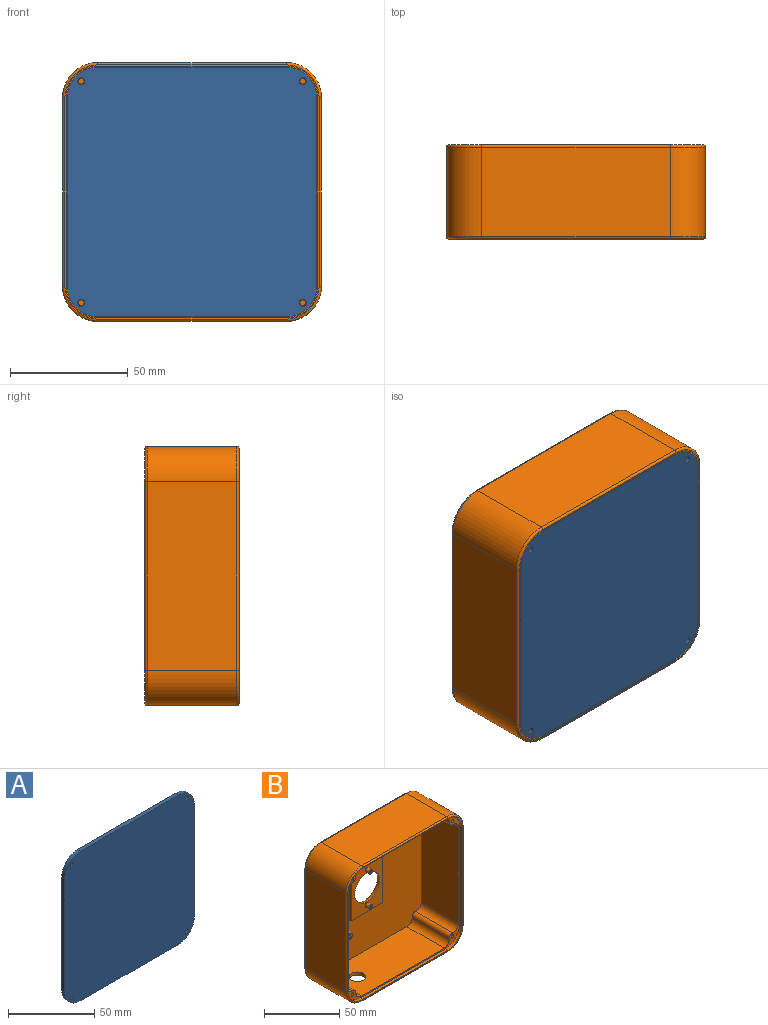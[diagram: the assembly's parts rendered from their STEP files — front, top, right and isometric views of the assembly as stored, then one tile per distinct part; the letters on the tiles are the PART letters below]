
ASSEMBLY  parts=2 mates=1
PART A: 14 faces, bbox 106x2.5x106 mm
  f0: plane 80x2.5mm, normal (-1,0,0), area 200mm2, adj f4,f5,f6,f9
  f1: plane 80x2.5mm, normal (0,0,-1), area 200mm2, adj f4,f5,f6,f7
  f2: plane 80x2.5mm, normal (1,0,0), area 200mm2, adj f4,f5,f7,f8
  f3: plane 80x2.5mm, normal (0,0,1), area 200mm2, adj f4,f5,f8,f9
  f4: plane 106x106mm, normal (0,-1,0), area 11062.7mm2, adj f0,f1,f2,f3,f6,f7,f8,f9
  f5: plane 106x106mm, normal (0,1,0), area 11062.7mm2, adj f0,f1,f2,f3,f6,f7,f8,f9
  f6: cylinder r=13mm len=13mm, axis (0,-1,0), area 51.1mm2, adj f0,f1,f4,f5
  f7: cylinder r=13mm len=13mm, axis (0,1,0), area 51.1mm2, adj f1,f2,f4,f5
  f8: cylinder r=13mm len=13mm, axis (0,-1,0), area 51.1mm2, adj f2,f3,f4,f5
  f9: cylinder r=13mm len=13mm, axis (0,1,0), area 51.1mm2, adj f0,f3,f4,f5
  f10: cylinder r=1.5mm len=3mm, axis (0,-1,0), area 23.6mm2, adj f4,f5
  f11: cylinder r=1.5mm len=3mm, axis (0,-1,0), area 23.6mm2, adj f4,f5
  f12: cylinder r=1.5mm len=3mm, axis (0,-1,0), area 23.6mm2, adj f4,f5
  f13: cylinder r=1.5mm len=3mm, axis (0,-1,0), area 23.6mm2, adj f4,f5
PART B: 91 faces, bbox 112.5x40x112.5 mm
  f0: cylinder r=3mm len=35mm, axis (0,1,0), area 176.2mm2, adj f1,f45,f83,f84
  f1: plane 107x107mm, normal (0,-1,0), area 566.8mm2, adj f0,f2,f4,f5,f7,f8,f9,f10
  f2: cylinder r=1.25mm len=35mm, axis (0,1,0), area 274.9mm2, adj f1,f82
  f3: plane 2.5x2.5mm, normal (0,-1,0), area 4.9mm2, adj f80
  f4: cylinder r=3mm len=35mm, axis (0,1,0), area 176.2mm2, adj f1,f45,f87,f88
  f5: cylinder r=1.25mm len=35mm, axis (0,1,0), area 274.9mm2, adj f1,f79
  f6: plane 2.5x2.5mm, normal (0,-1,0), area 4.9mm2, adj f77
  f7: plane 78.17x35mm, normal (0,0,-1), area 2735.8mm2, adj f1,f45,f88,f89
  f8: plane 78.17x35mm, normal (1,0,0), area 2735.8mm2, adj f1,f45,f86,f87
  f9: plane 78.17x35mm, normal (0,0,1), area 2640.7mm2, adj f1,f45,f54,f84,f85
  f10: plane 78.17x35mm, normal (-1,0,0), area 2735.8mm2, adj f1,f45,f83,f90
  f11: cone r=2.5mm half-angle=10deg, axis (0,1,0), area 151.3mm2, adj f12,f45
  f12: plane 5x5mm, normal (0,-1,0), area 14.7mm2, adj f11,f53
  f13: cone r=2.5mm half-angle=10deg, axis (0,1,0), area 151.3mm2, adj f14,f45
  f14: plane 5x5mm, normal (0,-1,0), area 14.7mm2, adj f13,f51
  f15: cone r=2.5mm half-angle=10deg, axis (0,1,0), area 151.3mm2, adj f16,f45
  f16: plane 5x5mm, normal (0,-1,0), area 14.7mm2, adj f15,f49
  f17: cone r=2.5mm half-angle=10deg, axis (0,1,0), area 151.3mm2, adj f18,f45
  f18: plane 5x5mm, normal (0,-1,0), area 14.7mm2, adj f17,f47
  f19: plane 80x38mm, normal (0,0,1), area 3040mm2, adj f25,f28,f35,f42
  f20: plane 80x38mm, normal (-1,0,0), area 3040mm2, adj f25,f26,f34,f43
  f21: plane 80x38mm, normal (0,0,-1), area 2945mm2, adj f26,f27,f30,f39,f54
  f22: plane 80x38mm, normal (1,0,0), area 3040mm2, adj f27,f28,f31,f38
  f23: plane 108x108mm, normal (0,1,0), area 10731.2mm2, adj f29,f30,f31,f32,f33,f34,f35,f36
  f24: plane 108x108mm, normal (0,-1,0), area 203.2mm2, adj f37,f38,f39,f40,f41,f42,f43,f44
  f25: cylinder r=15mm len=38mm, axis (0,1,0), area 895.4mm2, adj f19,f20,f36,f44
  f26: cylinder r=15mm len=38mm, axis (0,-1,0), area 895.4mm2, adj f20,f21,f32,f41
  f27: cylinder r=15mm len=38mm, axis (0,1,0), area 895.4mm2, adj f21,f22,f29,f37
  f28: cylinder r=15mm len=38mm, axis (0,-1,0), area 895.4mm2, adj f19,f22,f33,f40
  f29: torus R=14mm, axis (0,-1,0), area 36.1mm2, adj f23,f27,f30,f31
  f30: cylinder r=1mm len=80mm, axis (-1,0,0), area 125.7mm2, adj f21,f23,f29,f32
  f31: cylinder r=1mm len=80mm, axis (0,0,-1), area 125.7mm2, adj f22,f23,f29,f33
  f32: torus R=14mm, axis (0,-1,0), area 36.1mm2, adj f23,f26,f30,f34
  f33: torus R=14mm, axis (0,-1,0), area 36.1mm2, adj f23,f28,f31,f35
  f34: cylinder r=1mm len=80mm, axis (0,0,1), area 125.7mm2, adj f20,f23,f32,f36
  f35: cylinder r=1mm len=80mm, axis (1,0,0), area 125.7mm2, adj f19,f23,f33,f36
  f36: torus R=14mm, axis (0,-1,0), area 36.1mm2, adj f23,f25,f34,f35
  f37: torus R=14mm, axis (0,-1,0), area 36.1mm2, adj f24,f27,f38,f39
  f38: cylinder r=1mm len=80mm, axis (0,0,1), area 125.7mm2, adj f22,f24,f37,f40
  f39: cylinder r=1mm len=80mm, axis (1,0,0), area 125.7mm2, adj f21,f24,f37,f41
  f40: torus R=14mm, axis (0,-1,0), area 36.1mm2, adj f24,f28,f38,f42
  f41: torus R=14mm, axis (0,-1,0), area 36.1mm2, adj f24,f26,f39,f43
  f42: cylinder r=1mm len=80mm, axis (-1,0,0), area 125.7mm2, adj f19,f24,f40,f44
  f43: cylinder r=1mm len=80mm, axis (0,0,-1), area 125.7mm2, adj f20,f24,f41,f44
  f44: torus R=14mm, axis (0,-1,0), area 36.1mm2, adj f24,f25,f42,f43
  f45: plane 105x105mm, normal (0,-1,0), area 9322.5mm2, adj f0,f4,f7,f8,f9,f10,f11,f13
  f46: plane 2.5x2.5mm, normal (0,-1,0), area 4.9mm2, adj f47
  f47: cylinder r=1.25mm len=7.5mm, axis (0,-1,0), area 58.9mm2, adj f18,f46
  f48: plane 2.5x2.5mm, normal (0,-1,0), area 4.9mm2, adj f49
  f49: cylinder r=1.25mm len=7.5mm, axis (0,-1,0), area 58.9mm2, adj f16,f48
  f50: plane 2.5x2.5mm, normal (0,-1,0), area 4.9mm2, adj f51
  f51: cylinder r=1.25mm len=7.5mm, axis (0,-1,0), area 58.9mm2, adj f14,f50
  f52: plane 2.5x2.5mm, normal (0,-1,0), area 4.9mm2, adj f53
  f53: cylinder r=1.25mm len=7.5mm, axis (0,-1,0), area 58.9mm2, adj f12,f52
  f54: cylinder r=5.5mm len=11mm, axis (0,0,-1), area 86.4mm2, adj f9,f21
  f55: plane 40x1.5mm, normal (1,0,0), area 60mm2, adj f45,f56,f58,f59
  f56: plane 30x1.5mm, normal (0,0,1), area 45mm2, adj f45,f55,f57,f59
  f57: plane 40x1.5mm, normal (-1,0,0), area 60mm2, adj f45,f56,f58,f59
  f58: plane 30x1.5mm, normal (0,0,-1), area 45mm2, adj f45,f55,f57,f59
  f59: plane 40x30mm, normal (0,-1,0), area 758mm2, adj f55,f56,f57,f58,f60,f61,f63
  f60: torus R=15.6mm, axis (0,-1,0), area 515.3mm2, adj f23,f59
  f61: cylinder r=1.75mm len=3.5mm, axis (0,1,0), area 38.5mm2, adj f59,f62
  f62: plane 3.5x3.5mm, normal (0,-1,0), area 7.9mm2, adj f61,f67
  f63: cylinder r=1.75mm len=3.5mm, axis (0,1,0), area 38.5mm2, adj f59,f64
  f64: plane 3.5x3.5mm, normal (0,-1,0), area 7.9mm2, adj f63,f65
  f65: cylinder r=0.75mm len=5mm, axis (0,-1,0), area 23.6mm2, adj f64,f66
  f66: plane 1.5x1.5mm, normal (0,-1,0), area 1.8mm2, adj f65
  f67: cylinder r=0.75mm len=5mm, axis (0,-1,0), area 23.6mm2, adj f62,f68
  f68: plane 1.5x1.5mm, normal (0,-1,0), area 1.8mm2, adj f67
  f69: plane 80x2.5mm, normal (-1,0,0), area 200mm2, adj f1,f24,f70,f76
  f70: cylinder r=13.5mm len=13.5mm, axis (0,-1,0), area 53mm2, adj f1,f24,f69,f71
  f71: plane 80x2.5mm, normal (0,0,-1), area 200mm2, adj f1,f24,f70,f72
  f72: cylinder r=13.5mm len=13.5mm, axis (0,-1,0), area 53mm2, adj f1,f24,f71,f73
  f73: plane 80x2.5mm, normal (1,0,0), area 200mm2, adj f1,f24,f72,f74
  f74: cylinder r=13.5mm len=13.5mm, axis (0,-1,0), area 53mm2, adj f1,f24,f73,f75
  f75: plane 80x2.5mm, normal (0,0,1), area 200mm2, adj f1,f24,f74,f76
  f76: cylinder r=13.5mm len=13.5mm, axis (0,-1,0), area 53mm2, adj f1,f24,f69,f75
  f77: cylinder r=1.25mm len=35mm, axis (0,1,0), area 274.9mm2, adj f1,f6
  f78: cylinder r=3mm len=35mm, axis (0,1,0), area 176.2mm2, adj f1,f45,f89,f90
  f79: plane 2.5x2.5mm, normal (0,-1,0), area 4.9mm2, adj f5
  f80: cylinder r=1.25mm len=35mm, axis (0,1,0), area 274.9mm2, adj f1,f3
  f81: cylinder r=3mm len=35mm, axis (0,1,0), area 176.2mm2, adj f1,f45,f85,f86
  f82: plane 2.5x2.5mm, normal (0,-1,0), area 4.9mm2, adj f2
  f83: cylinder r=5mm len=35mm, axis (0,1,0), area 284.3mm2, adj f0,f1,f10,f45
  f84: cylinder r=5mm len=35mm, axis (0,1,0), area 284.3mm2, adj f0,f1,f9,f45
  f85: cylinder r=5mm len=35mm, axis (0,1,0), area 284.3mm2, adj f1,f9,f45,f81
  f86: cylinder r=5mm len=35mm, axis (0,1,0), area 284.3mm2, adj f1,f8,f45,f81
  f87: cylinder r=5mm len=35mm, axis (0,1,0), area 284.3mm2, adj f1,f4,f8,f45
  f88: cylinder r=5mm len=35mm, axis (0,1,0), area 284.3mm2, adj f1,f4,f7,f45
  f89: cylinder r=5mm len=35mm, axis (0,1,0), area 284.3mm2, adj f1,f7,f45,f78
  f90: cylinder r=5mm len=35mm, axis (0,1,0), area 284.3mm2, adj f1,f10,f45,f78
PLACE A rot(axis=(1,0,0),180deg) t=(-18,0,94.5)mm
PLACE B at identity
MATE fastened A.f4 <-> B.f60  axis (0,1,0) through (35,2.5,41.5)mm
